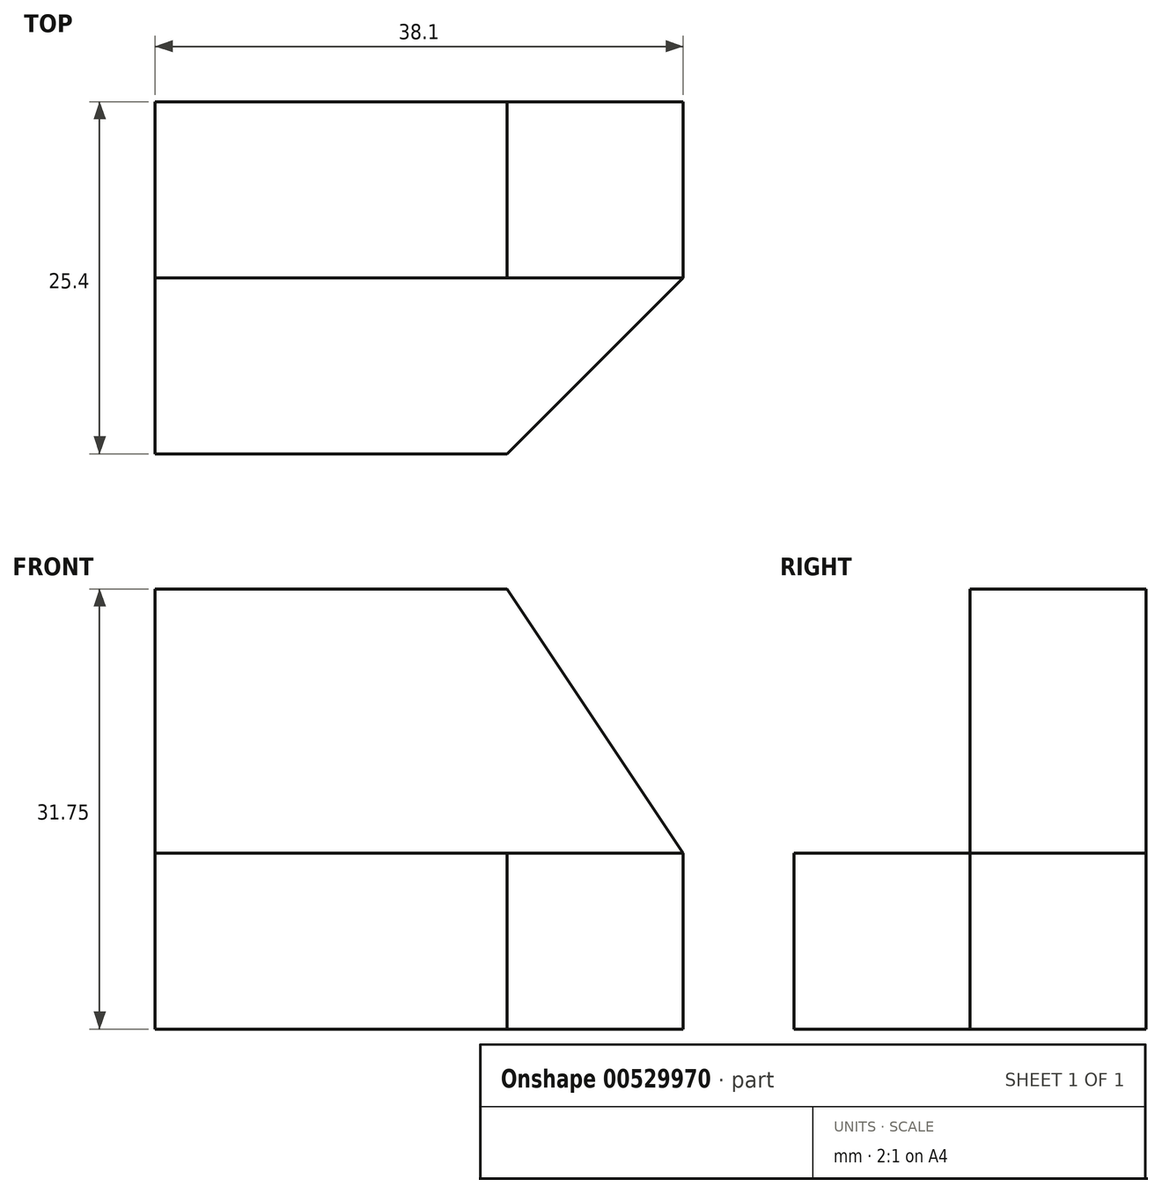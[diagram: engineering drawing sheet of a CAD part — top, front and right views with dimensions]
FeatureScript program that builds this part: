
annotation { "Feature Type Name" : "Feature", "Feature Type Description" : "" }
export const myFeature = defineFeature(function(context is Context, id is Id, definition is map)
    precondition{}
    {
        {
            var Q0;
            Q0=qCreatedBy(makeId("Right.planeOp"),FACE);
            var sketch = newSketch(context, id + "F0", { "sketchPlane" : qUnion([Q0])});
            skLineSegment(sketch, "E0", {"start": v(-35.16, 44.3) * mm, "end": v(-35.16, 25.26) * mm});
            skLineSegment(sketch, "E1", {"start": v(-35.16, 25.26) * mm, "end": v(-47.86, 25.26) * mm});
            skLineSegment(sketch, "E2", {"start": v(-47.86, 25.26) * mm, "end": v(-47.86, 12.56) * mm});
            skLineSegment(sketch, "E3", {"start": v(-47.86, 12.56) * mm, "end": v(-22.46, 12.56) * mm});
            skLineSegment(sketch, "E4", {"start": v(-22.46, 12.56) * mm, "end": v(-22.46, 44.3) * mm});
            skLineSegment(sketch, "E5", {"start": v(-22.46, 44.3) * mm, "end": v(-35.16, 44.3) * mm});
            skSolve(sketch);
        }
        {
            var Q0;
            Q0 = qSketchRegion(id + "F0", true);
            extrude(context, id + "F1", {"entities" : qUnion([Q0]), "depth" : 38.1 * mm, "offsetDistance" : 25.4 * mm});
        }
        {
            var Q0;
            Q0=makeQuery(id+"F1.opExtrude","SWEPT_FACE",FACE,{"disambiguationData":[OSD([sQuery(id+"F0.wireOp",EDGE,"E0")])]});
            var sketch = newSketch(context, id + "F2", { "sketchPlane" : qUnion([Q0])});
            skLineSegment(sketch, "E6", {"start": v(38.1, 44.3) * mm, "end": v(25.4, 44.3) * mm});
            skLineSegment(sketch, "E7", {"start": v(25.4, 44.3) * mm, "end": v(38.1, 25.26) * mm});
            skLineSegment(sketch, "E8", {"start": v(38.1, 25.26) * mm, "end": v(38.1, 44.3) * mm});
            skSolve(sketch);
        }
        {
            var Q0;
            Q0 = qSketchRegion(id + "F2", true);
            extrude(context, id + "F3", {"entities" : qUnion([Q0]), "operationType" : NewBodyOperationType.REMOVE, "oppositeDirection" : true, "depth" : 12.7 * mm, "offsetDistance" : 25.4 * mm});
        }
        {
            var Q0;
            Q0=makeQuery(id+"F1.opExtrude","SWEPT_FACE",FACE,{"disambiguationData":[OSD([sQuery(id+"F0.wireOp",EDGE,"E1")])]});
            var sketch = newSketch(context, id + "F4", { "sketchPlane" : qUnion([Q0])});
            skLineSegment(sketch, "E9", {"start": v(38.1, -35.16) * mm, "end": v(25.4, -47.86) * mm});
            skLineSegment(sketch, "E10", {"start": v(25.4, -47.86) * mm, "end": v(38.1, -47.86) * mm});
            skLineSegment(sketch, "E11", {"start": v(38.1, -47.86) * mm, "end": v(38.1, -35.16) * mm});
            skSolve(sketch);
        }
        {
            var Q0;
            Q0 = qSketchRegion(id + "F4", true);
            extrude(context, id + "F5", {"entities" : qUnion([Q0]), "operationType" : NewBodyOperationType.REMOVE, "oppositeDirection" : true, "depth" : 12.7 * mm, "offsetDistance" : 25.4 * mm});
        }
    });
